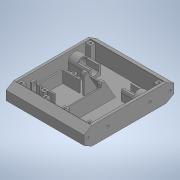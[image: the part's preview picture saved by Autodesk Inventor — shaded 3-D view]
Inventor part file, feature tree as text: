
AUTODESK INVENTOR PART (.ipt)
format: ipt  version: 2020 (Build 240168000, 168)  size: 649,216 bytes
history: native  units: in
note: dims shown in document units (in); Inventor stores cm internally (conversion verified against a paired STEP export)
features: extrude x19, sketch x19, projected_geometry x14, mirror x6, plane x1
ambient origin geometry x8: Origin, YZ Plane, XZ Plane, XY Plane, X Axis, Y Axis, Z Axis, Center Point
bodies: Solid1 (feature_tree)
feature tree (59):
  extrude  "Extrusion1"  Depth=5.9055in
  extrude  "Extrusion2"  TaperAngle=0.0deg  [1 undecoded]
  extrude  "Extrusion3"  Depth=1.063in
  extrude  "Extrusion4"  Depth=0.315in
  extrude  "Extrusion5"  TaperAngle=0.0deg  [1 undecoded]
  extrude  "Extrusion6"  Depth=0.5906in
  mirror  "Mirror1"
  extrude  "Extrusion7"  Depth=0.0787in
  mirror  "Mirror2"
  extrude  "Extrusion8"  Depth=0.6102in
  mirror  "Mirror3"
  plane  "Work Plane1"
  extrude  "Extrusion9"  Depth=0.7874in TaperAngle=0.0deg
  mirror  "Mirror4"
  extrude  "Extrusion10"  Depth=6.063in TaperAngle=0.0deg
  extrude  "Extrusion11"  Depth=0.1575in
  extrude  "Extrusion12"  TaperAngle=0.0deg  [1 undecoded]
  extrude  "Extrusion13"  Depth=0.2756in
  extrude  "Extrusion14"  Depth=0.4331in
  extrude  "Extrusion17"  Depth=2.7559in
  extrude  "Extrusion18"  Depth=0.0453in
  mirror  "Mirror6"
  extrude  "Extrusion19"  TaperAngle=0.0deg  [1 undecoded]
  mirror  "Mirror7"
  extrude  "Extrusion20"  Depth=0.0787in
  extrude  "Extrusion21"  Depth=0.993in
  sketch  "Sketch1"  dims[d0=1.1811in d1=5.9055in]
  sketch  "Sketch2"  dims[d2=5.1181in d3=0.0in]
  projected_geometry  "Projected Loop1"
  sketch  "Sketch3"  dims[d4=0.1575in d5=1.063in]
  projected_geometry  "Projected Loop2"
  projected_geometry  "Projected Loop3"
  sketch  "Sketch4"  dims[d6=0.0in d8=0.315in]
  sketch  "Sketch5"  dims[d10=0.993in d11=0.0in]
  projected_geometry  "Projected Loop4"
  sketch  "Sketch6"  dims[d12=0.6496in d13=0.5906in]
  sketch  "Sketch7"  dims[d14=1.5748in d15=0.0787in]
  sketch  "Sketch9"  dims[d16=0.5512in d17=0.0in d18=0.6102in]
  sketch  "Sketch10"  dims[d19=0.4803in d20=0.7874in d21=0.0in]
  sketch  "Sketch12"  dims[d22=0.1654in d23=6.063in d24=0.0in]
  projected_geometry  "Projected Loop6"
  projected_geometry  "Projected Loop7"
  projected_geometry  "Projected Loop8"
  sketch  "Sketch13"  dims[d25=0.5114in d26=0.1575in]
  sketch  "Sketch14"  dims[d27=1.5748in d28=0.0in d29=0.0in]
  sketch  "Sketch15"  dims[d30=0.1575in d31=0.2756in]
  projected_geometry  "Projected Loop15"
  sketch  "Sketch16"  dims[d32=0.0in d33=0.4331in]
  projected_geometry  "Projected Loop19"
  projected_geometry  "Projected Loop20"
  projected_geometry  "Projected Loop21"
  projected_geometry  "Projected Loop22"
  projected_geometry  "Projected Loop23"
  projected_geometry  "Projected Loop24"
  sketch  "Sketch20"  dims[d34=0.0906in d38=2.7559in]
  sketch  "Sketch21"  dims[d40=0.0453in d41=0.0909in]
  sketch  "Sketch22"  dims[d42=0.2362in d43=0.0in]
  sketch  "Sketch23"  dims[d44=60.0deg d45=0.0787in]
  sketch  "Sketch25"  dims[d46=0.315in d48=0.993in d49=0.0in d53=0.2756in d54=0.0in d55=0.4724in d56=1.1811in d57=1.5748in d58=1.5748in d59=0.0787in d60=0.0787in d62=0.315in d63=0.7677in d64=0.0in d66=0.1476in d67=0.2756in d68=0.0in d69=0.7874in d70=0.2953in d71=0.1181in d72=0.0in d89=0.0157in d90=0.0157in d91=0.1476in d92=0.1476in d96=0.315in d97=0.1575in d98=0.1181in d99=0.0in d102=0.1772in d104=0.3346in d105=135.0deg d106=0.2362in d107=0.0in d108=0.0394in d109=0.0in d110=0.063in d111=0.0394in d112=0.0in d117=0.993in d118=0.063in d119=0.3937in d120=0.0in]
note: 4 required parameter values undecoded (feature->parameter linkage not recoverable at this tier; creation-order binding heuristic only, values carry confidence <= 0.55)
